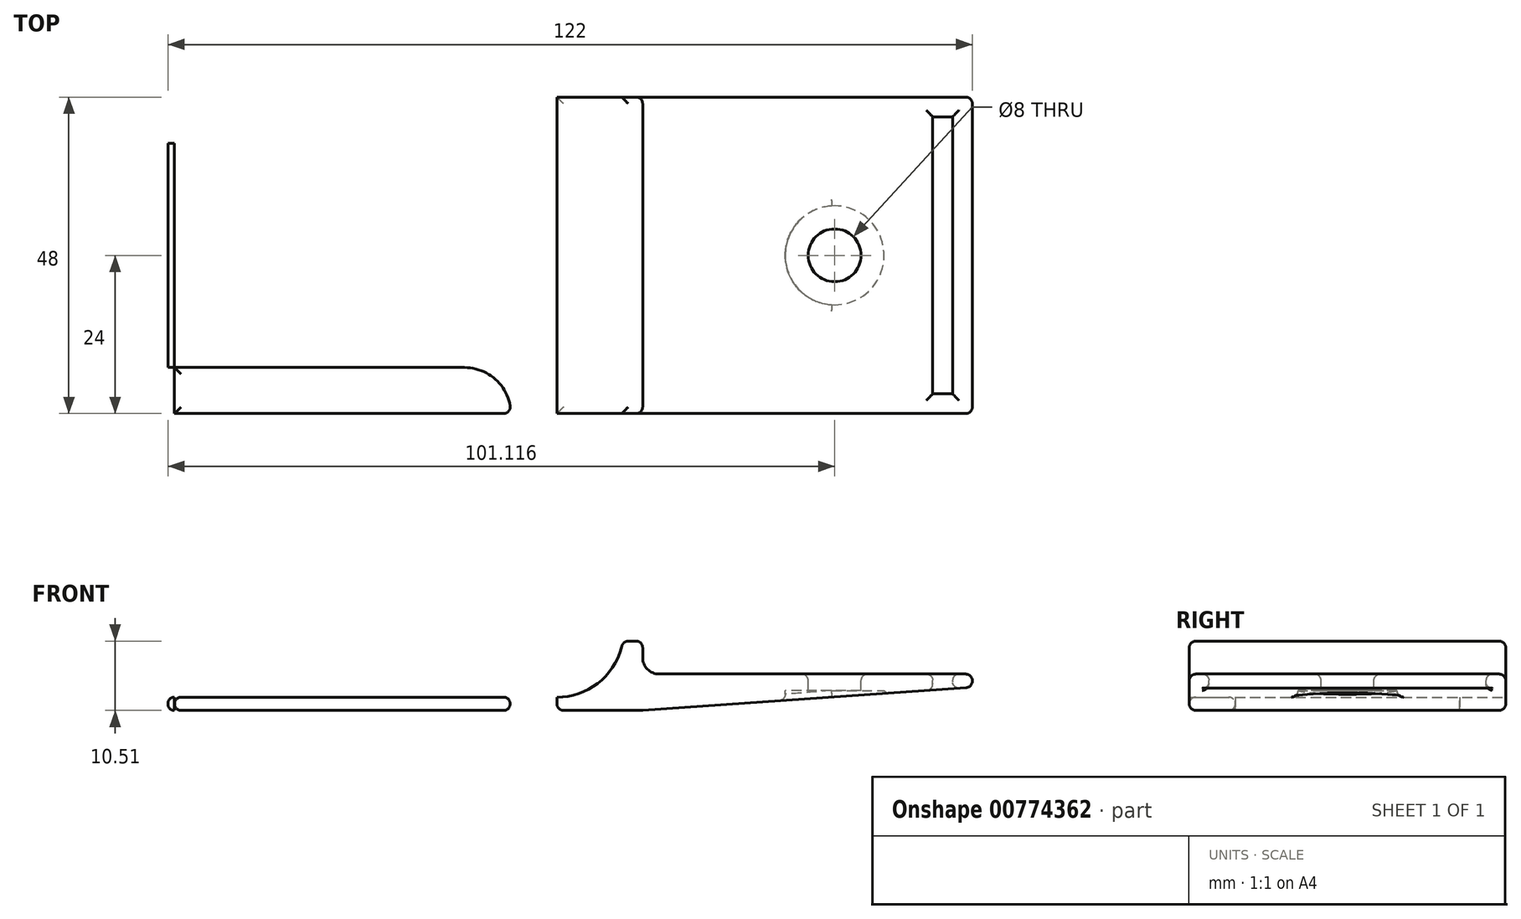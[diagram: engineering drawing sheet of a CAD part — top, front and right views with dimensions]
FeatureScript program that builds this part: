
annotation { "Feature Type Name" : "Feature", "Feature Type Description" : "" }
export const myFeature = defineFeature(function(context is Context, id is Id, definition is map)
    precondition{}
    {
        {
            var Q0;
            Q0=qCreatedBy(makeId("Front.planeOp"),FACE);
            var sketch = newSketch(context, id + "F0", { "sketchPlane" : qUnion([Q0])});
            skLineSegment(sketch, "E0", {"start": v(0, 1) * mm, "end": v(0, 1) * mm});
            skLineSegment(sketch, "E1", {"start": v(1, 2) * mm, "end": v(59, 2) * mm});
            skLineSegment(sketch, "E2", {"start": v(69, 10.51) * mm, "end": v(72, 10.51) * mm});
            skLineSegment(sketch, "E3", {"start": v(72, 10.51) * mm, "end": v(72, 8.01) * mm});
            skLineSegment(sketch, "E4", {"start": v(74.5, 5.51) * mm, "end": v(121, 5.51) * mm});
            skLineSegment(sketch, "E5", {"start": v(122, 4.51) * mm, "end": v(122, 4.45) * mm});
            skLineSegment(sketch, "E6", {"start": v(121.07, 3.45) * mm, "end": v(72, 0) * mm});
            skLineSegment(sketch, "E7", {"start": v(72, 0) * mm, "end": v(1, 0) * mm});
            skPoint(sketch, "E8.visualSharp", {"position": v(72, 5.51) * mm});
            skArc(sketch, "E8.filletArc", {"start": v(72, 8.01) * mm, "mid": v(72.73, 6.25) * mm, "end": v(74.5, 5.51) * mm});
            skPoint(sketch, "E9.visualSharp", {"position": v(0, 2) * mm});
            skArc(sketch, "E9.filletArc", {"start": v(1, 2) * mm, "mid": v(0.3, 1.7) * mm, "end": v(0, 1) * mm});
            skPoint(sketch, "E10.visualSharp", {"position": v(0, 0) * mm});
            skArc(sketch, "E10.filletArc", {"start": v(0, 1) * mm, "mid": v(0.3, 0.3) * mm, "end": v(1, 0) * mm});
            skPoint(sketch, "E11.visualSharp", {"position": v(122, 5.51) * mm});
            skArc(sketch, "E11.filletArc", {"start": v(122, 4.51) * mm, "mid": v(121.7, 5.22) * mm, "end": v(121, 5.51) * mm});
            skPoint(sketch, "E12.visualSharp", {"position": v(122, 3.51) * mm});
            skArc(sketch, "E12.filletArc", {"start": v(121.07, 3.45) * mm, "mid": v(121.73, 3.76) * mm, "end": v(122, 4.45) * mm});
            skArc(sketch, "E13", {"start": v(59, 2) * mm, "mid": v(65.57, 4.42) * mm, "end": v(69, 10.51) * mm});
            skSolve(sketch);
        }
        {
            var Q0;
            Q0=makeQuery(id+"F0.imprint","IMPRINT",FACE,{"disambiguationData":[TD([[makeQuery(id+"F0.imprint","IMPRINT",EDGE,{"derivedFrom":sQuery(id+"F0.wireOp",EDGE,"E1")}),-1.0]])]});
            extrude(context, id + "F1", {"entities" : qUnion([Q0]), "endBound" : BoundingType.SYMMETRIC, "depth" : 48 * mm, "offsetDistance" : 25 * mm});
        }
        {
            var Q0;
            Q0=makeQuery(id+"F1.opExtrude","SWEPT_FACE",FACE,{"disambiguationData":[OSD([sQuery(id+"F0.wireOp",EDGE,"E1")])]});
            var sketch = newSketch(context, id + "F2", { "sketchPlane" : qUnion([Q0])});
            skLineSegment(sketch, "E14", {"start": v(0, 0) * mm, "end": v(0, 17.01) * mm});
            skLineSegment(sketch, "E15", {"start": v(0, 17.01) * mm, "end": v(45, 17.01) * mm});
            skLineSegment(sketch, "E16", {"start": v(52, 24) * mm, "end": v(59, 24) * mm});
            skLineSegment(sketch, "E17", {"start": v(59, 24) * mm, "end": v(59, 0) * mm});
            skArc(sketch, "E18", {"start": v(45, 17.01) * mm, "mid": v(49.94, 19.06) * mm, "end": v(52, 24) * mm});
            skLineSegment(sketch, "E19.bottom", {"start": v(3, 14.01) * mm, "end": v(45, 14.01) * mm});
            skLineSegment(sketch, "E19.top", {"start": v(3, 11.01) * mm, "end": v(45, 11.01) * mm});
            skLineSegment(sketch, "E19.left", {"start": v(3, 14.01) * mm, "end": v(3, 11.01) * mm});
            skLineSegment(sketch, "E19.right", {"start": v(45, 14.01) * mm, "end": v(45, 11.01) * mm});
            skLineSegment(sketch, "E20.MirrorCS", {"start": v(3, -11.01) * mm, "end": v(45, -11.01) * mm});
            skLineSegment(sketch, "E21.MirrorCS", {"start": v(3, -14.01) * mm, "end": v(3, -11.01) * mm});
            skLineSegment(sketch, "E22.MirrorCS", {"start": v(3, -14.01) * mm, "end": v(45, -14.01) * mm});
            skLineSegment(sketch, "E23.MirrorCS", {"start": v(45, -14.01) * mm, "end": v(45, -11.01) * mm});
            skArc(sketch, "E24.MirrorCS", {"start": v(45, -17.01) * mm, "mid": v(49.94, -19.06) * mm, "end": v(52, -24) * mm});
            skLineSegment(sketch, "E25.MirrorCS", {"start": v(52, -24) * mm, "end": v(59, -24) * mm});
            skLineSegment(sketch, "E26.MirrorCS", {"start": v(59, -24) * mm, "end": v(59, 0) * mm});
            skLineSegment(sketch, "E27.MirrorCS", {"start": v(0, -17.01) * mm, "end": v(45, -17.01) * mm});
            skLineSegment(sketch, "E28.MirrorCS", {"start": v(0, 0) * mm, "end": v(0, -17.01) * mm});
            skLineSegment(sketch, "E29", {"start": v(0, -17.01) * mm, "end": v(0, -24) * mm});
            skLineSegment(sketch, "E30", {"start": v(0, -24) * mm, "end": v(52, -24) * mm});
            skLineSegment(sketch, "E31", {"start": v(0, 17.01) * mm, "end": v(0, 24) * mm});
            skLineSegment(sketch, "E32", {"start": v(0, 24) * mm, "end": v(52, 24) * mm});
            skSolve(sketch);
        }
        {
            var Q0;
            {var subQ0=sQuery(id+"F2.wireOp",EDGE,"E18");Q0=makeQuery(id+"F2.imprint","IMPRINT",FACE,{"disambiguationData":[TD([[makeQuery(id+"F2.imprint","IMPRINT",EDGE,{"derivedFrom":subQ0}),1.0]])]});}
            var Q1;
            {var subQ0=sQuery(id+"F2.wireOp",EDGE,"E24.MirrorCS");Q1=makeQuery(id+"F2.imprint","IMPRINT",FACE,{"disambiguationData":[TD([[makeQuery(id+"F2.imprint","IMPRINT",EDGE,{"derivedFrom":subQ0}),-1.0]])]});}
            var Q2;
            Q2=makeQuery(id+"F2.imprint","IMPRINT",FACE,{"disambiguationData":[TD([[makeQuery(id+"F2.imprint","IMPRINT",EDGE,{"derivedFrom":sQuery(id+"F2.wireOp",EDGE,"E20.MirrorCS")}),-1.0]])]});
            var Q3;
            Q3=makeQuery(id+"F2.imprint","IMPRINT",FACE,{"disambiguationData":[TD([[makeQuery(id+"F2.imprint","IMPRINT",EDGE,{"derivedFrom":sQuery(id+"F2.wireOp",EDGE,"E19.bottom")}),-1.0]])]});
            var Q4;
            {var subQ0=sQuery(id+"F2.wireOp",EDGE,"E31");Q4=makeQuery(id+"F2.imprint","IMPRINT",FACE,{"disambiguationData":[TD([[makeQuery(id+"F2.imprint","IMPRINT",EDGE,{"derivedFrom":subQ0}),-1.0]])]});}
            var Q5;
            {var subQ0=sQuery(id+"F2.wireOp",EDGE,"E29");Q5=makeQuery(id+"F2.imprint","IMPRINT",FACE,{"disambiguationData":[TD([[makeQuery(id+"F2.imprint","IMPRINT",EDGE,{"derivedFrom":subQ0}),1.0]])]});}
            extrude(context, id + "F3", {"entities" : qUnion([Q0, Q1, Q2, Q3, Q4, Q5]), "operationType" : NewBodyOperationType.REMOVE, "oppositeDirection" : true, "depth" : 25 * mm, "offsetDistance" : 25 * mm});
        }
        {
            var Q0;
            Q0=makeQuery(id+"F1.opExtrude","SWEPT_FACE",FACE,{"disambiguationData":[OSD([sQuery(id+"F0.wireOp",EDGE,"E4")])]});
            var sketch = newSketch(context, id + "F4", { "sketchPlane" : qUnion([Q0])});
            skLineSegment(sketch, "E33.bottom", {"start": v(119, 21) * mm, "end": v(116, 21) * mm});
            skLineSegment(sketch, "E33.top", {"start": v(119, -21) * mm, "end": v(116, -21) * mm});
            skLineSegment(sketch, "E33.left", {"start": v(119, 21) * mm, "end": v(119, -21) * mm});
            skLineSegment(sketch, "E33.right", {"start": v(116, 21) * mm, "end": v(116, -21) * mm});
            skLineSegment(sketch, "E34", {"start": v(74.5, 0) * mm, "end": v(101.12, 0) * mm, "construction": true});
            skPoint(sketch, "E34.endSnap0", {"position": v(121, 0) * mm});
            skLineSegment(sketch, "E35", {"start": v(101.12, 0) * mm, "end": v(125.67, 0) * mm, "construction": true});
            skCircle(sketch, "E36", {"center": v(101.12, 0) * mm, "radius": 4 * mm});
            skCircle(sketch, "E37", {"center": v(101.12, 0) * mm, "radius": 7.5 * mm});
            skSolve(sketch);
        }
        {
            var Q0;
            Q0=makeQuery(id+"F4.imprint","IMPRINT",FACE,{"disambiguationData":[TD([[makeQuery(id+"F4.imprint","IMPRINT",EDGE,{"derivedFrom":sQuery(id+"F4.wireOp",EDGE,"E33.bottom")}),1.0]])]});
            extrude(context, id + "F5", {"entities" : qUnion([Q0]), "operationType" : NewBodyOperationType.REMOVE, "oppositeDirection" : true, "depth" : 25 * mm, "offsetDistance" : 25 * mm});
        }
        {
            var Q0;
            Q0=makeQuery(id+"F4.imprint","IMPRINT",FACE,{"disambiguationData":[TD([[makeQuery(id+"F4.imprint","IMPRINT",EDGE,{"derivedFrom":sQuery(id+"F4.wireOp",EDGE,"E36")}),1.0]])]});
            extrude(context, id + "F6", {"entities" : qUnion([Q0]), "operationType" : NewBodyOperationType.REMOVE, "oppositeDirection" : true, "depth" : 25 * mm, "offsetDistance" : 25 * mm});
        }
        {
            var Q0;
            Q0=makeQuery(id+"F4.imprint","IMPRINT",FACE,{"disambiguationData":[TD([[makeQuery(id+"F4.imprint","IMPRINT",EDGE,{"derivedFrom":sQuery(id+"F4.wireOp",EDGE,"E36")}),-1.0]])]});
            extrude(context, id + "F7", {"entities" : qUnion([Q0]), "operationType" : NewBodyOperationType.REMOVE, "oppositeDirection" : true, "depth" : 50 * mm, "offsetDistance" : 25 * mm, "hasSecondDirection" : true, "secondDirectionOppositeDirection" : true, "secondDirectionDepth" : 2.5 * mm});
        }
        {
            var Q0;
            Q0=makeQuery(id+"F1.opExtrude","SWEPT_FACE",FACE,{"disambiguationData":[OSD([sQuery(id+"F0.wireOp",EDGE,"E1")])]});
            var Q1;
            Q1=makeQuery(id+"F1.opExtrude","SWEPT_FACE",FACE,{"disambiguationData":[OSD([sQuery(id+"F0.wireOp",EDGE,"E7")])]});
            var Q2;
            Q2=makeQuery(id+"F1.opExtrude","SWEPT_FACE",FACE,{"disambiguationData":[OSD([sQuery(id+"F0.wireOp",EDGE,"E4")])]});
            var Q3;
            Q3=makeQuery(id+"F1.opExtrude","SWEPT_EDGE",EDGE,{"disambiguationData":[OSD([sQuery(id+"F0.wireOp",EDGE,"E2"),sQuery(id+"F0.wireOp",EDGE,"E3")])]});
            var Q4;
            Q4=makeQuery(id+"F1.opExtrude","SWEPT_EDGE",EDGE,{"disambiguationData":[OSD([sQuery(id+"F0.wireOp",EDGE,"E2"),sQuery(id+"F0.wireOp",EDGE,"E13")])]});
            var Q5;
            Q5=makeQuery(id+"F1.opExtrude","SWEPT_FACE",FACE,{"disambiguationData":[OSD([sQuery(id+"F0.wireOp",EDGE,"E6")])]});
            var Q6;
            Q6=makeQuery(id+"F1.opExtrude","CAP_EDGE",EDGE,{"disambiguationData":[OSD([sQuery(id+"F0.wireOp",EDGE,"E2")])],"isStart":false});
            var Q7;
            Q7=makeQuery(id+"F1.opExtrude","CAP_EDGE",EDGE,{"disambiguationData":[OSD([sQuery(id+"F0.wireOp",EDGE,"E2")])],"isStart":true});
            var Q8;
            Q8=makeQuery(id+"F3.boolean.opBoolean","COPY",EDGE,{"derivedFrom":makeQuery(id+"F3.opExtrude","SWEPT_EDGE",EDGE,{"disambiguationData":[OSD([sQuery(id+"F2.wireOp",EDGE,"E24.MirrorCS"),sQuery(id+"F2.wireOp",EDGE,"E25.MirrorCS"),sQuery(id+"F2.wireOp",EDGE,"E30")])]})});
            var Q9;
            Q9=makeQuery(id+"F3.boolean.opBoolean","COPY",EDGE,{"derivedFrom":makeQuery(id+"F3.opExtrude","SWEPT_EDGE",EDGE,{"disambiguationData":[OSD([sQuery(id+"F2.wireOp",EDGE,"E16"),sQuery(id+"F2.wireOp",EDGE,"E18"),sQuery(id+"F2.wireOp",EDGE,"E32")])]})});
            fillet(context, id + "F8", {"entities" : qUnion([Q0, Q1, Q2, Q3, Q4, Q5, Q6, Q7, Q8, Q9]), "radius" : 1 * mm, "tangentPropagation" : true, "allowEdgeOverflow" : false});
        }
    });
